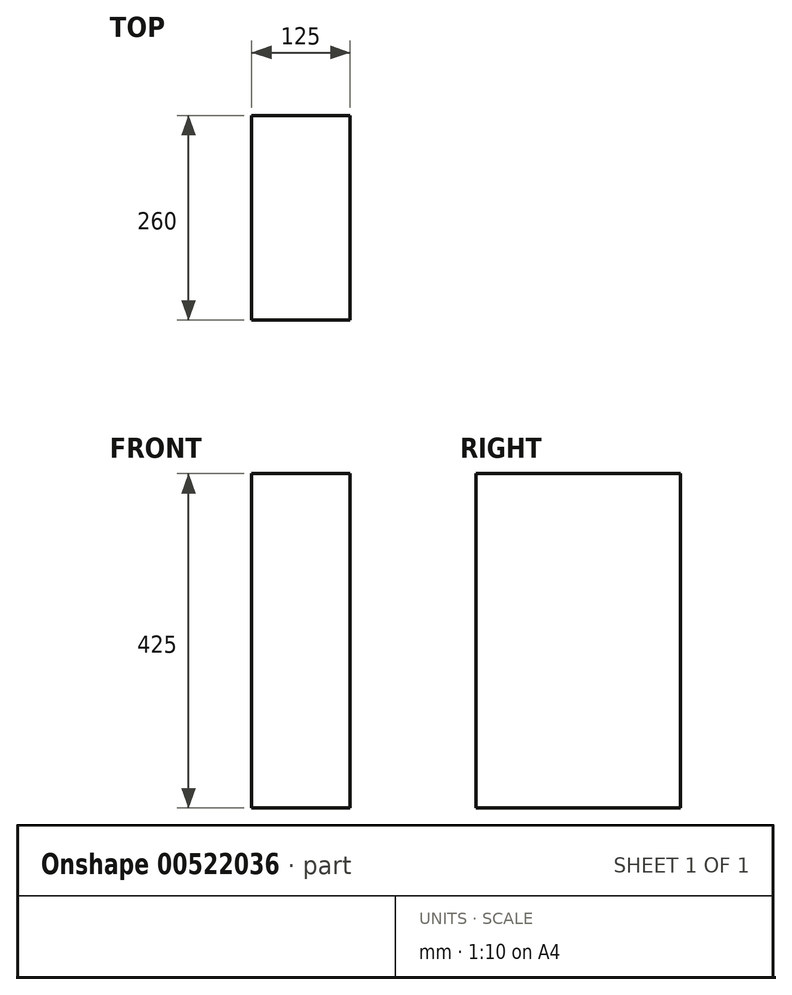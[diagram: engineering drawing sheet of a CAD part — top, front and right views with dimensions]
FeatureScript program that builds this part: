
annotation { "Feature Type Name" : "Feature", "Feature Type Description" : "" }
export const myFeature = defineFeature(function(context is Context, id is Id, definition is map)
    precondition{}
    {
        {
            var Q0;
            Q0=qCreatedBy(makeId("Top.planeOp"),FACE);
            var sketch = newSketch(context, id + "F0", { "sketchPlane" : qUnion([Q0])});
            skLineSegment(sketch, "E0.bottom", {"start": v(0, 0) * mm, "end": v(125, 0) * mm});
            skLineSegment(sketch, "E0.top", {"start": v(0, 260) * mm, "end": v(125, 260) * mm});
            skLineSegment(sketch, "E0.left", {"start": v(0, 0) * mm, "end": v(0, 260) * mm});
            skLineSegment(sketch, "E0.right", {"start": v(125, 0) * mm, "end": v(125, 260) * mm});
            skSolve(sketch);
        }
        {
            var Q0;
            Q0=makeQuery(id+"F0.imprint","IMPRINT",FACE,{"disambiguationData":[TD([[makeQuery(id+"F0.imprint","IMPRINT",EDGE,{"derivedFrom":sQuery(id+"F0.wireOp",EDGE,"E0.bottom")}),1.0]])]});
            extrude(context, id + "F1", {"entities" : qUnion([Q0]), "depth" : 425 * mm, "offsetDistance" : 25 * mm});
        }
    });
